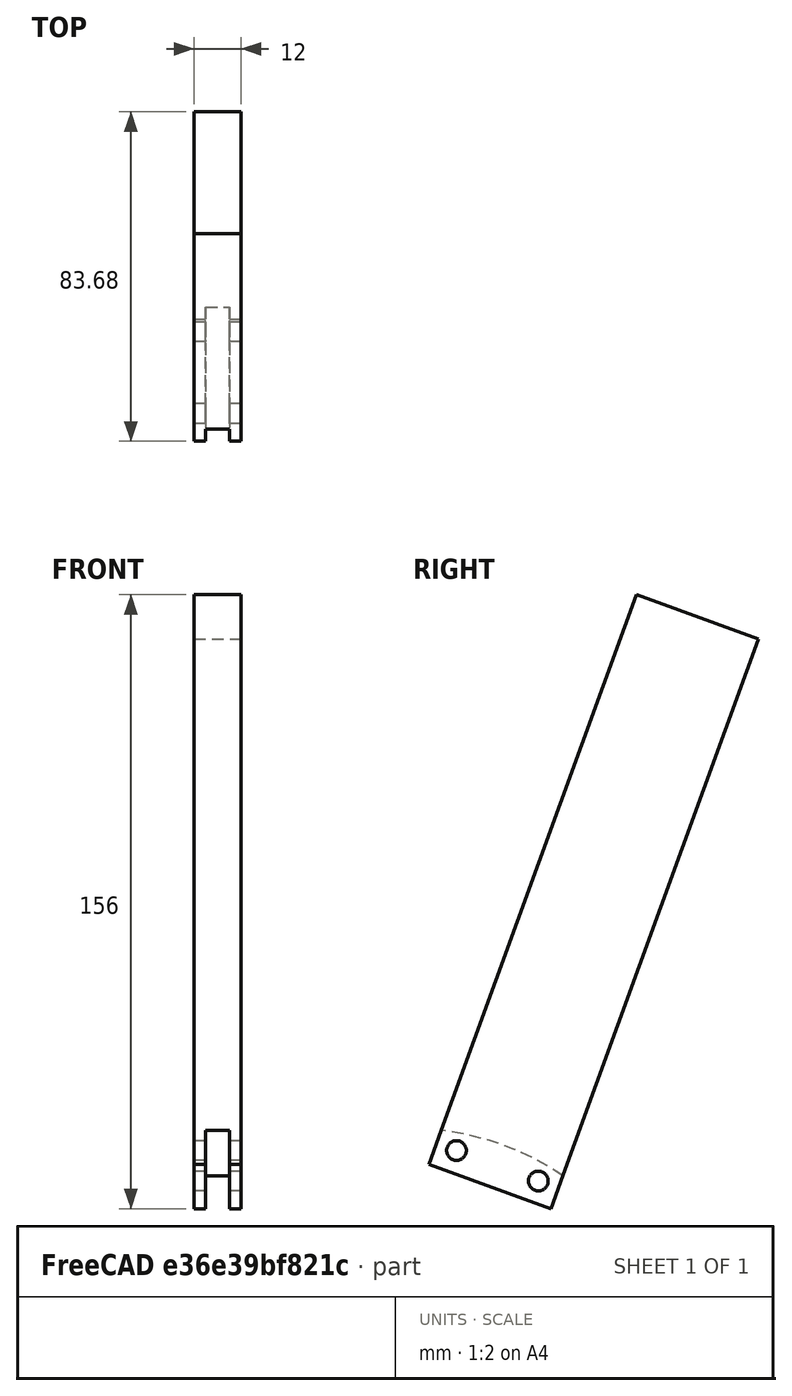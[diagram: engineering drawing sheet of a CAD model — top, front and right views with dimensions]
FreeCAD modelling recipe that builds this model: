
FCSTD DOCUMENT  (FreeCAD 0.18R16110 (Git))
Label: hand
License: All rights reserved
LicenseURL: http://en.wikipedia.org/wiki/All_rights_reserved
objects: Part::Cylinder×3, Part::Cut×3, Sketcher::SketchObject×1, Part::Extrusion×1, Mesh::Feature×1
note: 8 computed .brp shape members not serialized (recipe doc carries the construction recipe); baked Part::Feature solids carry a one-line shape summary decoded from their .brp

FEATURE [Sketcher::SketchObject] Sketch
  sketch-geometry (6):
    g0: LineSegment StartX=-6 StartY=0 StartZ=0 EndX=6 EndY=-2e-16 EndZ=0
    g1: LineSegment StartX=6 StartY=-2e-16 StartZ=0 EndX=6 EndY=9 EndZ=0
    g2: LineSegment StartX=-6 StartY=154 StartZ=0 EndX=-6 EndY=9 EndZ=0
    g3: LineSegment StartX=-6 StartY=9 StartZ=0 EndX=-6 EndY=0 EndZ=0
    g4: LineSegment StartX=-6 StartY=154 StartZ=0 EndX=6 EndY=154 EndZ=0
    g5: LineSegment StartX=6 StartY=154 StartZ=0 EndX=6 EndY=9 EndZ=0
  constraints (16):
    c: PointOnObject(g0,g-1)
    c: Coincident(g0,g1)
    c: Vertical(g1)
    c: Coincident(g2,g3)
    c: Coincident(g3,g0)
    c: Symmetric(g0,g0,g-2)
    c: Symmetric(g2,g1,g-2)
    c: DistanceX(g0,g0) = 12
    c: DistanceY(g3,g3) = 9
    c: DistanceX(g2) = -6
    c: Distance(g2) = 145
    c: Coincident(g2,g4)
    c: Coincident(g4,g5)
    c: Coincident(g5,g1)
    c: Vertical(g5)
    c: Horizontal(g4)
FEATURE [Part::Extrusion] Extrude
  Base = -> Sketch
  Dir = (0,0,1)
  DirMode = 2
  FaceMakerClass = Part::FaceMakerBullseye
  LengthFwd = 33
  LengthRev = 0
  Solid = true
  Symmetric = false
FEATURE [Part::Cylinder] Cylinder
  Angle = 360
  AttacherType = Attacher::AttachEngine3D
  Height = 6.1
  Placement = pos=(-3,-59,17) rot=(0,1,0;1.5708rad)
  Radius = 70
FEATURE [Part::Cut] Cut
  Base = -> Extrude
  Placement = pos=(0,36.22,49.58) rot=(1,0,0;1.22173rad)
  Tool = -> Cylinder
FEATURE [Part::Cylinder] Cylinder001
  Angle = 360
  AttacherType = Attacher::AttachEngine3D
  Height = 15
  Placement = pos=(7.5,33,56.6) rot=(0,-1,0;1.5708rad)
  Radius = 2.5
FEATURE [Part::Cylinder] Cylinder002
  Angle = 360
  AttacherType = Attacher::AttachEngine3D
  Height = 15
  Placement = pos=(7.5,12.2,64.35) rot=(0,-1,0;1.5708rad)
  Radius = 2.5
FEATURE [Part::Cut] Cut001
  Base = -> Cut
  Tool = -> Cylinder001
FEATURE [Part::Cut] Cut002
  Base = -> Cut001
  Tool = -> Cylinder002
FEATURE [Mesh::Feature] armscrew
  Placement = pos=(0,0,-3.2) rot=(0,0,1;0rad)
